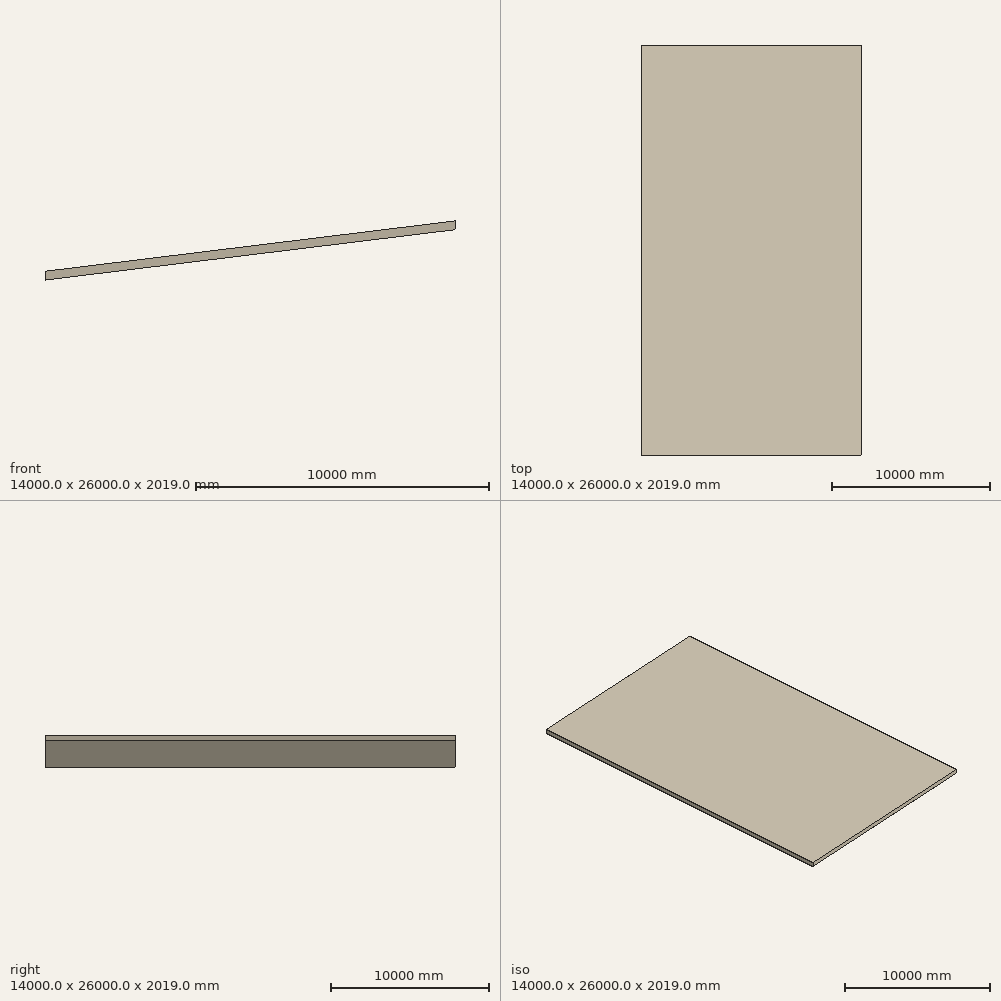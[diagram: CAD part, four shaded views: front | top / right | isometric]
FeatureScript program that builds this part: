
annotation { "Feature Type Name" : "Feature", "Feature Type Description" : "" }
export const myFeature = defineFeature(function(context is Context, id is Id, definition is map)
    precondition{}
    {
        {
            var Q0;
            Q0=qCreatedBy(makeId("Front.planeOp"),FACE);
            var sketch = newSketch(context, id + "F0", { "sketchPlane" : qUnion([Q0])});
            skLineSegment(sketch, "E0.bottom", {"start": v(0, 0) * mm, "end": v(14000, 0) * mm});
            skLineSegment(sketch, "E0.top", {"start": v(0, 5000) * mm, "end": v(14000, 5000) * mm});
            skLineSegment(sketch, "E0.left", {"start": v(0, 0) * mm, "end": v(0, 5000) * mm});
            skLineSegment(sketch, "E0.right", {"start": v(14000, 0) * mm, "end": v(14000, 5000) * mm});
            skSolve(sketch);
        }
        {
            var Q0;
            Q0=makeQuery(id+"F0.imprint","IMPRINT",FACE,{"disambiguationData":[TD([[makeQuery(id+"F0.imprint","IMPRINT",EDGE,{"derivedFrom":sQuery(id+"F0.wireOp",EDGE,"E0.bottom")}),1.0]])]});
            var sketch = newSketch(context, id + "F1", { "sketchPlane" : qUnion([Q0])});
            skLineSegment(sketch, "E1", {"start": v(0, 0) * mm, "end": v(16385.35, 2011.87) * mm});
            skLineSegment(sketch, "E2", {"start": v(16385.35, 2011.87) * mm, "end": v(15350.92, -2206.42) * mm});
            skLineSegment(sketch, "E3", {"start": v(15350.92, -2206.42) * mm, "end": v(0, 0) * mm});
            skSolve(sketch);
        }
        {
            var Q0;
            Q0=makeQuery(id+"F0.imprint","IMPRINT",FACE,{"disambiguationData":[TD([[makeQuery(id+"F0.imprint","IMPRINT",EDGE,{"derivedFrom":sQuery(id+"F0.wireOp",EDGE,"E0.bottom")}),1.0]])]});
            extrude(context, id + "F2", {"entities" : qUnion([Q0]), "oppositeDirection" : true, "depth" : 26000 * mm});
        }
        {
            var Q0;
            {var subQ1=makeQuery(id+"F0.imprint","IMPRINT",EDGE,{"derivedFrom":sQuery(id+"F0.wireOp",EDGE,"E0.bottom")});Q0=makeQuery(id+"F1.imprint","IMPRINT",FACE,{"disambiguationData":[TD([[makeQuery(id+"F1.imprint","IMPRINT",EDGE,{"derivedFrom":subQ1}),1.0]])]});}
            extrude(context, id + "F3", {"entities" : qUnion([Q0]), "operationType" : NewBodyOperationType.REMOVE, "endBound" : BoundingType.THROUGH_ALL, "oppositeDirection" : true, "depth" : 25 * mm});
        }
        {
            var Q0;
            Q0=makeQuery(id+"F2.opExtrude","CAP_FACE",FACE,{"disambiguationData":[OSD([sQuery(id+"F0.wireOp",EDGE,"E0.bottom"),sQuery(id+"F0.wireOp",EDGE,"E0.top"),sQuery(id+"F0.wireOp",EDGE,"E0.left"),sQuery(id+"F0.wireOp",EDGE,"E0.right")])],"isStart":true});
            var sketch = newSketch(context, id + "F4", { "sketchPlane" : qUnion([Q0])});
            skLineSegment(sketch, "E4", {"start": v(0, 300) * mm, "end": v(14000, 2018.98) * mm});
            skLineSegment(sketch, "E5", {"start": v(14000, 2018.98) * mm, "end": v(14000, 5950.09) * mm});
            skLineSegment(sketch, "E6", {"start": v(14000, 5950.09) * mm, "end": v(0, 6246.22) * mm});
            skLineSegment(sketch, "E7", {"start": v(0, 6246.22) * mm, "end": v(0, 300) * mm});
            skSolve(sketch);
        }
        {
            var Q0;
            {var subQ0=sQuery(id+"F4.wireOp",EDGE,"E4");Q0=makeQuery(id+"F4.imprint","IMPRINT",FACE,{"disambiguationData":[TD([[makeQuery(id+"F4.imprint","IMPRINT",EDGE,{"derivedFrom":subQ0}),1.0]])]});}
            extrude(context, id + "F5", {"entities" : qUnion([Q0]), "operationType" : NewBodyOperationType.REMOVE, "endBound" : BoundingType.THROUGH_ALL, "oppositeDirection" : true, "depth" : 25 * mm});
        }
    });
